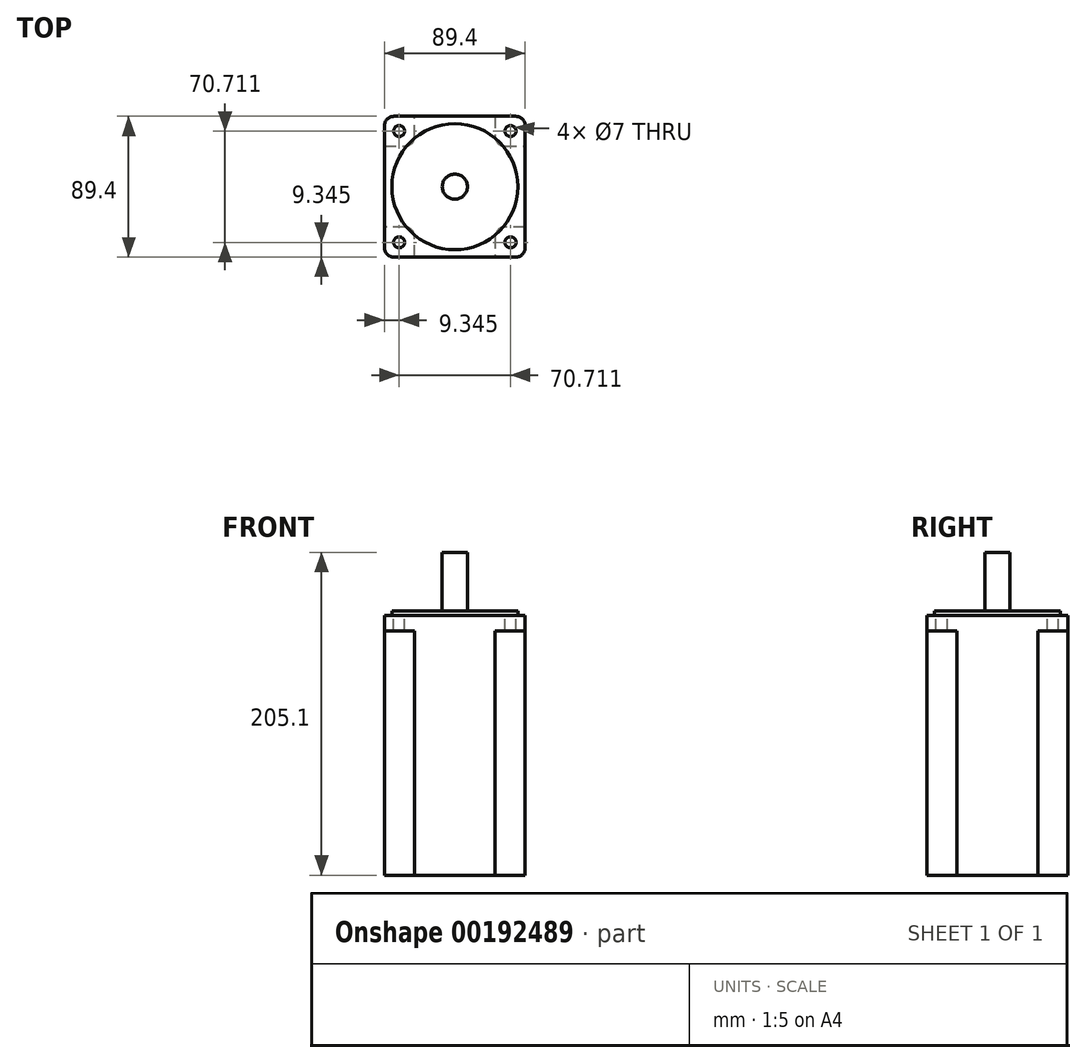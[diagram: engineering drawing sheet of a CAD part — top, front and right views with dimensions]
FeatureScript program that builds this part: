
annotation { "Feature Type Name" : "Feature", "Feature Type Description" : "" }
export const myFeature = defineFeature(function(context is Context, id is Id, definition is map)
    precondition{}
    {
        {
            var Q0;
            Q0=qCreatedBy(makeId("Top.planeOp"),FACE);
            var sketch = newSketch(context, id + "F0", { "sketchPlane" : qUnion([Q0])});
            skCircle(sketch, "E0", {"center": v(0, 0) * mm, "radius": 40 * mm});
            skSolve(sketch);
        }
        {
            var Q0;
            Q0 = qSketchRegion(id + "F0", true);
            extrude(context, id + "F1", {"entities" : qUnion([Q0]), "depth" : 2.74 * mm});
        }
        {
            var Q0;
            Q0=makeQuery(id+"F1.opExtrude","CAP_FACE",FACE,{"disambiguationData":[OSD([sQuery(id+"F0.wireOp",EDGE,"E0")])],"isStart":true});
            var sketch = newSketch(context, id + "F2", { "sketchPlane" : qUnion([Q0])});
            skCircle(sketch, "E1", {"center": v(0, 0) * mm, "radius": 8 * mm});
            skSolve(sketch);
        }
        {
            var Q0;
            Q0 = qSketchRegion(id + "F2", true);
            extrude(context, id + "F3", {"entities" : qUnion([Q0]), "operationType" : NewBodyOperationType.ADD, "oppositeDirection" : true, "depth" : 40 * mm});
        }
        {
            var Q0;
            Q0=makeQuery(id+"F1.opExtrude","CAP_FACE",FACE,{"disambiguationData":[OSD([sQuery(id+"F0.wireOp",EDGE,"E0")])],"isStart":true});
            var sketch = newSketch(context, id + "F4", { "sketchPlane" : qUnion([Q0])});
            skLineSegment(sketch, "E2.bottom", {"start": v(38.7, -44.7) * mm, "end": v(-38.7, -44.7) * mm});
            skLineSegment(sketch, "E2.top", {"start": v(38.7, 44.7) * mm, "end": v(-38.7, 44.7) * mm});
            skLineSegment(sketch, "E2.left", {"start": v(44.7, -38.7) * mm, "end": v(44.7, 38.7) * mm});
            skLineSegment(sketch, "E2.right", {"start": v(-44.7, -38.7) * mm, "end": v(-44.7, 38.7) * mm});
            skPoint(sketch, "E2.middle", {"position": v(0, 0) * mm});
            skCircle(sketch, "E3", {"center": v(-35.36, 35.36) * mm, "radius": 3.5 * mm});
            skCircle(sketch, "E4.1.0", {"center": v(-35.36, -35.36) * mm, "radius": 3.5 * mm});
            skCircle(sketch, "E4.2.0", {"center": v(35.36, -35.36) * mm, "radius": 3.5 * mm});
            skCircle(sketch, "E4.3.0", {"center": v(35.36, 35.36) * mm, "radius": 3.5 * mm});
            skPoint(sketch, "E5.visualSharp", {"position": v(-44.7, 44.7) * mm});
            skArc(sketch, "E5.filletArc", {"start": v(-38.7, 44.7) * mm, "mid": v(-42.94, 42.94) * mm, "end": v(-44.7, 38.7) * mm});
            skPoint(sketch, "E6.visualSharp", {"position": v(-44.7, -44.7) * mm});
            skArc(sketch, "E6.filletArc", {"start": v(-44.7, -38.7) * mm, "mid": v(-42.94, -42.94) * mm, "end": v(-38.7, -44.7) * mm});
            skPoint(sketch, "E7.visualSharp", {"position": v(44.7, -44.7) * mm});
            skArc(sketch, "E7.filletArc", {"start": v(38.7, -44.7) * mm, "mid": v(42.94, -42.94) * mm, "end": v(44.7, -38.7) * mm});
            skPoint(sketch, "E8.visualSharp", {"position": v(44.7, 44.7) * mm});
            skArc(sketch, "E8.filletArc", {"start": v(44.7, 38.7) * mm, "mid": v(42.94, 42.94) * mm, "end": v(38.7, 44.7) * mm});
            skSolve(sketch);
        }
        {
            var Q0;
            Q0 = qSketchRegion(id + "F4", true);
            extrude(context, id + "F5", {"entities" : qUnion([Q0]), "operationType" : NewBodyOperationType.ADD, "depth" : 9.9 * mm});
        }
        {
            var Q0;
            Q0=makeQuery(id+"F5.opExtrude","CAP_FACE",FACE,{"disambiguationData":[OSD([sQuery(id+"F4.wireOp",EDGE,"E2.bottom"),sQuery(id+"F4.wireOp",EDGE,"E2.top"),sQuery(id+"F4.wireOp",EDGE,"E2.left"),sQuery(id+"F4.wireOp",EDGE,"E2.right"),sQuery(id+"F4.wireOp",EDGE,"E3"),sQuery(id+"F4.wireOp",EDGE,"E4.1.0"),sQuery(id+"F4.wireOp",EDGE,"E4.2.0"),sQuery(id+"F4.wireOp",EDGE,"E4.3.0"),sQuery(id+"F4.wireOp",EDGE,"E5.filletArc"),sQuery(id+"F4.wireOp",EDGE,"E6.filletArc"),sQuery(id+"F4.wireOp",EDGE,"E7.filletArc"),sQuery(id+"F4.wireOp",EDGE,"E8.filletArc")])],"isStart":false});
            var sketch = newSketch(context, id + "F6", { "sketchPlane" : qUnion([Q0])});
            skLineSegment(sketch, "E9", {"start": v(44.7, 25.65) * mm, "end": v(31.65, 25.65) * mm});
            skLineSegment(sketch, "E10", {"start": v(25.65, 31.65) * mm, "end": v(25.65, 44.7) * mm});
            skLineSegment(sketch, "E11", {"start": v(25.65, 44.7) * mm, "end": v(0, 44.7) * mm});
            skLineSegment(sketch, "E12", {"start": v(0, 44.7) * mm, "end": v(0, 0) * mm});
            skLineSegment(sketch, "E13", {"start": v(0, 0) * mm, "end": v(44.7, 0) * mm});
            skLineSegment(sketch, "E14", {"start": v(44.7, 0) * mm, "end": v(44.7, 25.65) * mm});
            skPoint(sketch, "E15.visualSharp", {"position": v(25.65, 25.65) * mm});
            skArc(sketch, "E15.filletArc", {"start": v(25.65, 31.65) * mm, "mid": v(27.4, 27.4) * mm, "end": v(31.65, 25.65) * mm});
            skLineSegment(sketch, "E16.1.0", {"start": v(-31.65, 25.65) * mm, "end": v(-44.7, 25.65) * mm});
            skArc(sketch, "E16.1.1", {"start": v(-31.65, 25.65) * mm, "mid": v(-27.4, 27.4) * mm, "end": v(-25.65, 31.65) * mm});
            skLineSegment(sketch, "E16.1.2", {"start": v(-25.65, 44.7) * mm, "end": v(-25.65, 31.65) * mm});
            skLineSegment(sketch, "E16.1.3", {"start": v(0, 44.7) * mm, "end": v(-25.65, 44.7) * mm});
            skLineSegment(sketch, "E16.1.4", {"start": v(0, 0) * mm, "end": v(0, 44.7) * mm});
            skLineSegment(sketch, "E16.1.5", {"start": v(-44.7, 0) * mm, "end": v(0, 0) * mm});
            skLineSegment(sketch, "E16.1.6", {"start": v(-44.7, 25.65) * mm, "end": v(-44.7, 0) * mm});
            skLineSegment(sketch, "E16.2.0", {"start": v(-25.65, -31.65) * mm, "end": v(-25.65, -44.7) * mm});
            skArc(sketch, "E16.2.1", {"start": v(-25.65, -31.65) * mm, "mid": v(-27.4, -27.4) * mm, "end": v(-31.65, -25.65) * mm});
            skLineSegment(sketch, "E16.2.2", {"start": v(-44.7, -25.65) * mm, "end": v(-31.65, -25.65) * mm});
            skLineSegment(sketch, "E16.2.3", {"start": v(-44.7, 0) * mm, "end": v(-44.7, -25.65) * mm});
            skLineSegment(sketch, "E16.2.4", {"start": v(0, 0) * mm, "end": v(-44.7, 0) * mm});
            skLineSegment(sketch, "E16.2.5", {"start": v(0, -44.7) * mm, "end": v(0, 0) * mm});
            skLineSegment(sketch, "E16.2.6", {"start": v(-25.65, -44.7) * mm, "end": v(0, -44.7) * mm});
            skLineSegment(sketch, "E16.3.0", {"start": v(31.65, -25.65) * mm, "end": v(44.7, -25.65) * mm});
            skArc(sketch, "E16.3.1", {"start": v(31.65, -25.65) * mm, "mid": v(27.4, -27.4) * mm, "end": v(25.65, -31.65) * mm});
            skLineSegment(sketch, "E16.3.2", {"start": v(25.65, -44.7) * mm, "end": v(25.65, -31.65) * mm});
            skLineSegment(sketch, "E16.3.3", {"start": v(0, -44.7) * mm, "end": v(25.65, -44.7) * mm});
            skLineSegment(sketch, "E16.3.4", {"start": v(0, 0) * mm, "end": v(0, -44.7) * mm});
            skLineSegment(sketch, "E16.3.5", {"start": v(44.7, 0) * mm, "end": v(0, 0) * mm});
            skLineSegment(sketch, "E16.3.6", {"start": v(44.7, -25.65) * mm, "end": v(44.7, 0) * mm});
            skPoint(sketch, "E16.center", {"position": v(0, 0) * mm});
            skSolve(sketch);
        }
        {
            var Q0;
            Q0 = qSketchRegion(id + "F6", true);
            extrude(context, id + "F7", {"entities" : qUnion([Q0]), "operationType" : NewBodyOperationType.ADD, "depth" : 155.2 * mm});
        }
    });
